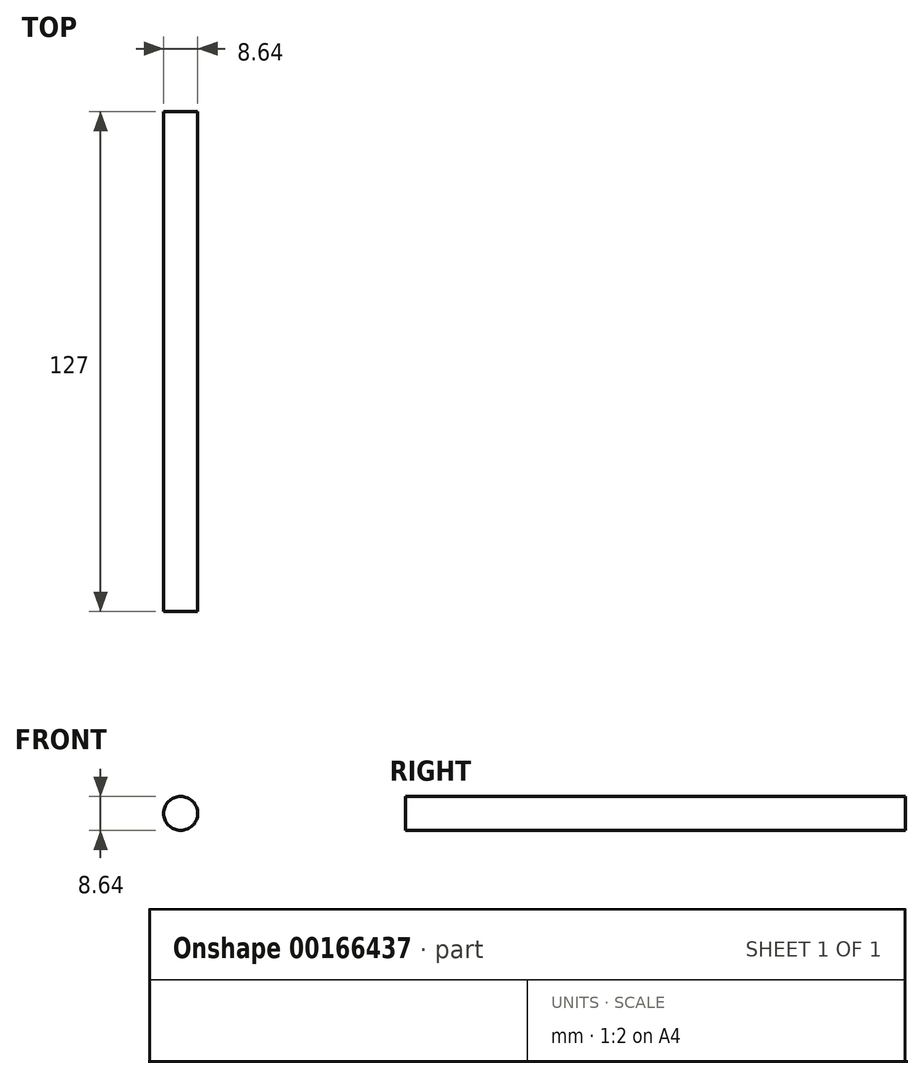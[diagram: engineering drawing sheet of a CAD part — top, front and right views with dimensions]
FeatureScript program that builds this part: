
annotation { "Feature Type Name" : "Feature", "Feature Type Description" : "" }
export const myFeature = defineFeature(function(context is Context, id is Id, definition is map)
    precondition{}
    {
        {
            var Q0;
            Q0=qCreatedBy(makeId("Front.planeOp"),FACE);
            var sketch = newSketch(context, id + "F0", { "sketchPlane" : qUnion([Q0])});
            skCircle(sketch, "E0", {"center": v(0, 0) * mm, "radius": 4.32 * mm});
            skCircle(sketch, "E1", {"center": v(0, 0) * mm, "radius": 4.45 * mm});
            skSolve(sketch);
        }
        {
            var Q0;
            Q0=makeQuery(id+"F0.imprint","IMPRINT",FACE,{"disambiguationData":[TD([[makeQuery(id+"F0.imprint","IMPRINT",EDGE,{"derivedFrom":sQuery(id+"F0.wireOp",EDGE,"E0")}),1.0]])]});
            extrude(context, id + "F1", {"entities" : qUnion([Q0]), "endBound" : BoundingType.SYMMETRIC, "depth" : 127 * mm});
        }
    });
